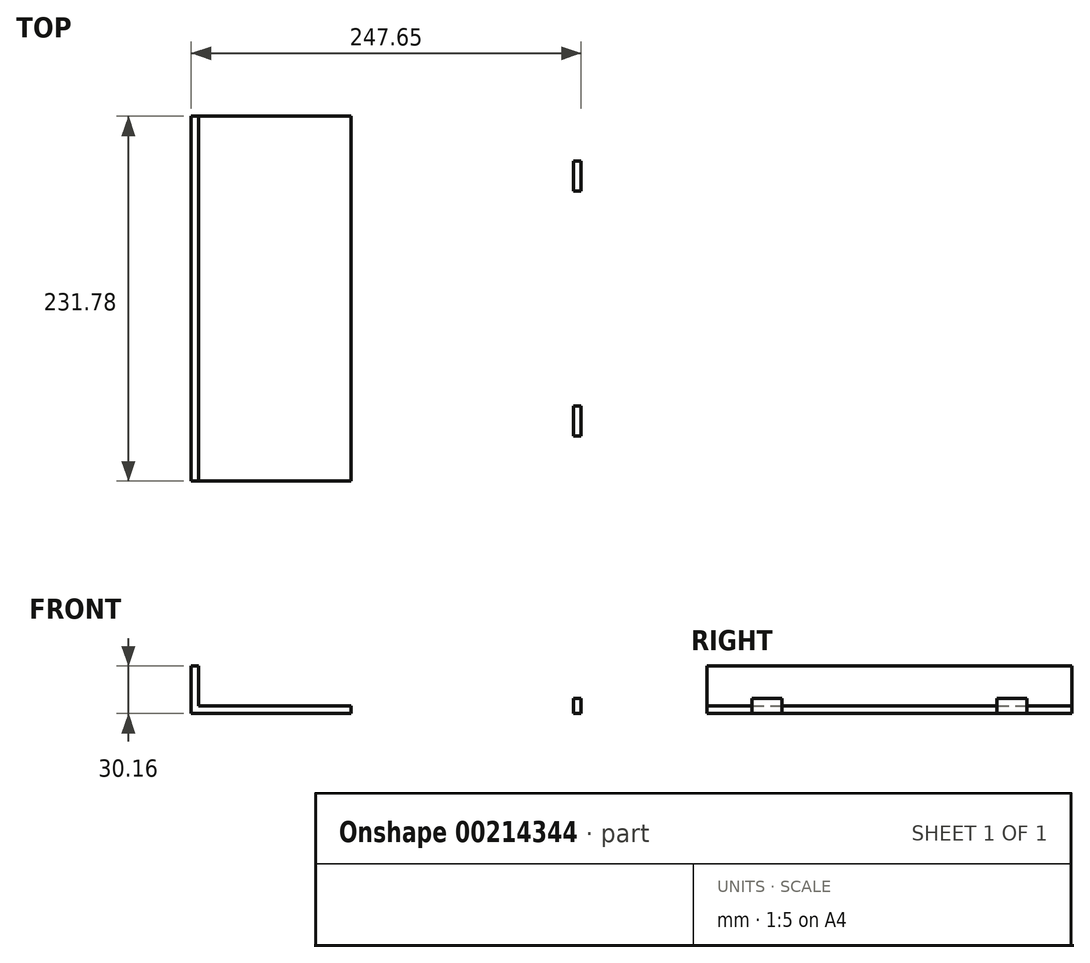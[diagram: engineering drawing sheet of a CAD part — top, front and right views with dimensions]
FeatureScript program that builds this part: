
annotation { "Feature Type Name" : "Feature", "Feature Type Description" : "" }
export const myFeature = defineFeature(function(context is Context, id is Id, definition is map)
    precondition{}
    {
        {
            var Q0;
            Q0=qCreatedBy(makeId("Top.planeOp"),FACE);
            var sketch = newSketch(context, id + "F0", { "sketchPlane" : qUnion([Q0])});
            skLineSegment(sketch, "E0.bottom", {"start": v(76.2, -116.74) * mm, "end": v(-76.2, -116.74) * mm});
            skLineSegment(sketch, "E0.top", {"start": v(76.2, 116.74) * mm, "end": v(-76.2, 116.74) * mm});
            skLineSegment(sketch, "E0.left", {"start": v(76.2, -116.74) * mm, "end": v(76.2, 116.74) * mm});
            skLineSegment(sketch, "E0.right", {"start": v(-76.2, -116.74) * mm, "end": v(-76.2, 116.74) * mm});
            skPoint(sketch, "E0.middle", {"position": v(0, 0) * mm});
            skLineSegment(sketch, "E1.0", {"start": v(101.6, 142.14) * mm, "end": v(-101.6, 142.14) * mm});
            skLineSegment(sketch, "E1.1", {"start": v(101.6, -142.14) * mm, "end": v(101.6, 142.14) * mm});
            skLineSegment(sketch, "E1.2", {"start": v(101.6, -142.14) * mm, "end": v(-101.6, -142.14) * mm});
            skLineSegment(sketch, "E1.3", {"start": v(-101.6, -142.14) * mm, "end": v(-101.6, 142.14) * mm});
            skLineSegment(sketch, "E2.bottom", {"start": v(-101.6, 142.14) * mm, "end": v(101.6, 142.14) * mm});
            skLineSegment(sketch, "E2.top", {"start": v(-101.6, 167.54) * mm, "end": v(101.6, 167.54) * mm});
            skLineSegment(sketch, "E2.left", {"start": v(-101.6, 142.14) * mm, "end": v(-101.6, 167.54) * mm});
            skLineSegment(sketch, "E2.right", {"start": v(101.6, 142.14) * mm, "end": v(101.6, 167.54) * mm});
            skLineSegment(sketch, "E3.bottom", {"start": v(-101.6, -142.14) * mm, "end": v(101.6, -142.14) * mm});
            skLineSegment(sketch, "E3.top", {"start": v(-101.6, -167.54) * mm, "end": v(101.6, -167.54) * mm});
            skLineSegment(sketch, "E3.left", {"start": v(-101.6, -142.14) * mm, "end": v(-101.6, -167.54) * mm});
            skLineSegment(sketch, "E3.right", {"start": v(101.6, -142.14) * mm, "end": v(101.6, -167.54) * mm});
            skLineSegment(sketch, "E4.bottom", {"start": v(76.2, 116.74) * mm, "end": v(63.5, 116.74) * mm});
            skLineSegment(sketch, "E4.top", {"start": v(76.2, 129.44) * mm, "end": v(63.5, 129.44) * mm});
            skLineSegment(sketch, "E4.left", {"start": v(76.2, 116.74) * mm, "end": v(76.2, 129.44) * mm});
            skLineSegment(sketch, "E4.right", {"start": v(63.5, 116.74) * mm, "end": v(63.5, 129.44) * mm});
            skLineSegment(sketch, "E5.bottom", {"start": v(76.2, -116.74) * mm, "end": v(63.5, -116.74) * mm});
            skLineSegment(sketch, "E5.top", {"start": v(76.2, -129.44) * mm, "end": v(63.5, -129.44) * mm});
            skLineSegment(sketch, "E5.left", {"start": v(76.2, -116.74) * mm, "end": v(76.2, -129.44) * mm});
            skLineSegment(sketch, "E5.right", {"start": v(63.5, -116.74) * mm, "end": v(63.5, -129.44) * mm});
            skLineSegment(sketch, "E6.bottom", {"start": v(76.2, 115.89) * mm, "end": v(-177.8, 115.89) * mm});
            skLineSegment(sketch, "E6.top", {"start": v(76.2, -115.89) * mm, "end": v(-177.8, -115.89) * mm});
            skLineSegment(sketch, "E6.left", {"start": v(76.2, 115.89) * mm, "end": v(76.2, -115.89) * mm});
            skLineSegment(sketch, "E6.right", {"start": v(-177.8, 115.89) * mm, "end": v(-177.8, -115.89) * mm});
            skLineSegment(sketch, "E7", {"start": v(-177.8, 0) * mm, "end": v(76.2, 0) * mm, "construction": true});
            skSolve(sketch);
        }
        {
            var Q0;
            {var subQ5=sQuery(id+"F0.wireOp",EDGE,"E6.right");Q0=makeQuery(id+"F0.imprint","IMPRINT",FACE,{"disambiguationData":[TD([[makeQuery(id+"F0.imprint","IMPRINT",EDGE,{"derivedFrom":subQ5}),1.0]])]});}
            var Q1;
            {var subQ0=sQuery(id+"F0.wireOp",EDGE,"E6.top");var subQ1=sQuery(id+"F0.wireOp",EDGE,"E0.right");var subQ2=makeQuery(id+"F0.imprint","INTERSECT",VERTEX,{"derivedFrom":[subQ1,subQ0]});Q1=makeQuery(id+"F0.imprint","IMPRINT",FACE,{"disambiguationData":[TD([[makeQuery(id+"F0.imprint","IMPRINT",EDGE,{"disambiguationData":[TD([[subQ2,-1.0]])],"derivedFrom":subQ1}),1.0]])]});}
            var Q2;
            {var subQ5=sQuery(id+"F0.wireOp",EDGE,"E6.left");Q2=makeQuery(id+"F0.imprint","IMPRINT",FACE,{"disambiguationData":[TD([[makeQuery(id+"F0.imprint","IMPRINT",EDGE,{"derivedFrom":subQ5}),-1.0]])]});}
            extrude(context, id + "F1", {"entities" : qUnion([Q0, Q1, Q2]), "depth" : 4.76 * mm});
        }
        {
            var Q0;
            Q0=makeQuery(id+"F1.opExtrude","CAP_FACE",FACE,{"disambiguationData":[OSD([sQuery(id+"F0.wireOp",EDGE,"E6.bottom"),sQuery(id+"F0.wireOp",EDGE,"E6.top"),sQuery(id+"F0.wireOp",EDGE,"E6.left"),sQuery(id+"F0.wireOp",EDGE,"E6.right")])],"isStart":false});
            var sketch = newSketch(context, id + "F2", { "sketchPlane" : qUnion([Q0])});
            skLineSegment(sketch, "E8.bottom", {"start": v(-177.8, 115.89) * mm, "end": v(-173.04, 115.89) * mm});
            skLineSegment(sketch, "E8.top", {"start": v(-177.8, -115.89) * mm, "end": v(-173.04, -115.89) * mm});
            skLineSegment(sketch, "E8.left", {"start": v(-177.8, 115.89) * mm, "end": v(-177.8, -115.89) * mm});
            skLineSegment(sketch, "E8.right", {"start": v(-173.04, 115.89) * mm, "end": v(-173.04, -115.89) * mm});
            skSolve(sketch);
        }
        {
            var Q0;
            Q0 = qSketchRegion(id + "F2", true);
            extrude(context, id + "F3", {"entities" : qUnion([Q0]), "operationType" : NewBodyOperationType.ADD, "depth" : 25.4 * mm});
        }
        {
            var Q0;
            Q0=makeQuery(id+"F1.opExtrude","CAP_FACE",FACE,{"disambiguationData":[OSD([sQuery(id+"F0.wireOp",EDGE,"E6.bottom"),sQuery(id+"F0.wireOp",EDGE,"E6.top"),sQuery(id+"F0.wireOp",EDGE,"E6.left"),sQuery(id+"F0.wireOp",EDGE,"E6.right")])],"isStart":true});
            var sketch = newSketch(context, id + "F4", { "sketchPlane" : qUnion([Q0])});
            skLineSegment(sketch, "E9.bottom", {"start": v(76.2, 77.79) * mm, "end": v(50.8, 77.79) * mm});
            skLineSegment(sketch, "E9.top", {"start": v(76.2, -77.79) * mm, "end": v(50.8, -77.79) * mm});
            skLineSegment(sketch, "E9.left", {"start": v(76.2, 77.79) * mm, "end": v(76.2, -77.79) * mm});
            skLineSegment(sketch, "E10", {"start": v(50.8, 77.79) * mm, "end": v(46.04, 77.79) * mm});
            skLineSegment(sketch, "E11", {"start": v(46.04, 77.79) * mm, "end": v(46.04, -77.79) * mm});
            skLineSegment(sketch, "E12", {"start": v(46.04, -77.79) * mm, "end": v(50.8, -77.79) * mm});
            skLineSegment(sketch, "E13", {"start": v(50.8, 77.79) * mm, "end": v(50.8, -77.79) * mm});
            skLineSegment(sketch, "E14", {"start": v(69.85, 87.31) * mm, "end": v(65.09, 87.31) * mm});
            skLineSegment(sketch, "E15", {"start": v(65.09, 87.31) * mm, "end": v(65.09, 68.26) * mm});
            skLineSegment(sketch, "E16", {"start": v(65.09, 68.26) * mm, "end": v(69.85, 68.26) * mm});
            skLineSegment(sketch, "E17", {"start": v(69.85, 68.26) * mm, "end": v(69.85, 87.31) * mm});
            skLineSegment(sketch, "E18", {"start": v(0, 0) * mm, "end": v(76.2, 0) * mm, "construction": true});
            skLineSegment(sketch, "E19.MirrorCS", {"start": v(69.85, -87.31) * mm, "end": v(65.09, -87.31) * mm});
            skLineSegment(sketch, "E20.MirrorCS", {"start": v(65.09, -87.31) * mm, "end": v(65.09, -68.26) * mm});
            skLineSegment(sketch, "E21.MirrorCS", {"start": v(69.85, -68.26) * mm, "end": v(69.85, -87.31) * mm});
            skLineSegment(sketch, "E22.MirrorCS", {"start": v(65.09, -68.26) * mm, "end": v(69.85, -68.26) * mm});
            skSolve(sketch);
        }
        {
            var Q0;
            {var subQ5=sQuery(id+"F4.wireOp",EDGE,"E16");Q0=makeQuery(id+"F4.imprint","IMPRINT",FACE,{"disambiguationData":[TD([[makeQuery(id+"F4.imprint","IMPRINT",EDGE,{"derivedFrom":subQ5}),1.0]])]});}
            var Q1;
            {var subQ5=sQuery(id+"F4.wireOp",EDGE,"E22.MirrorCS");Q1=makeQuery(id+"F4.imprint","IMPRINT",FACE,{"disambiguationData":[TD([[makeQuery(id+"F4.imprint","IMPRINT",EDGE,{"derivedFrom":subQ5}),-1.0]])]});}
            var Q2;
            {var subQ5=sQuery(id+"F4.wireOp",EDGE,"E14");Q2=makeQuery(id+"F4.imprint","IMPRINT",FACE,{"disambiguationData":[TD([[makeQuery(id+"F4.imprint","IMPRINT",EDGE,{"derivedFrom":subQ5}),1.0]])]});}
            var Q3;
            {var subQ5=sQuery(id+"F4.wireOp",EDGE,"E19.MirrorCS");Q3=makeQuery(id+"F4.imprint","IMPRINT",FACE,{"disambiguationData":[TD([[makeQuery(id+"F4.imprint","IMPRINT",EDGE,{"derivedFrom":subQ5}),-1.0]])]});}
            extrude(context, id + "F5", {"entities" : qUnion([Q0, Q1, Q2, Q3]), "operationType" : NewBodyOperationType.ADD, "oppositeDirection" : true, "depth" : 9.52 * mm});
        }
    });
